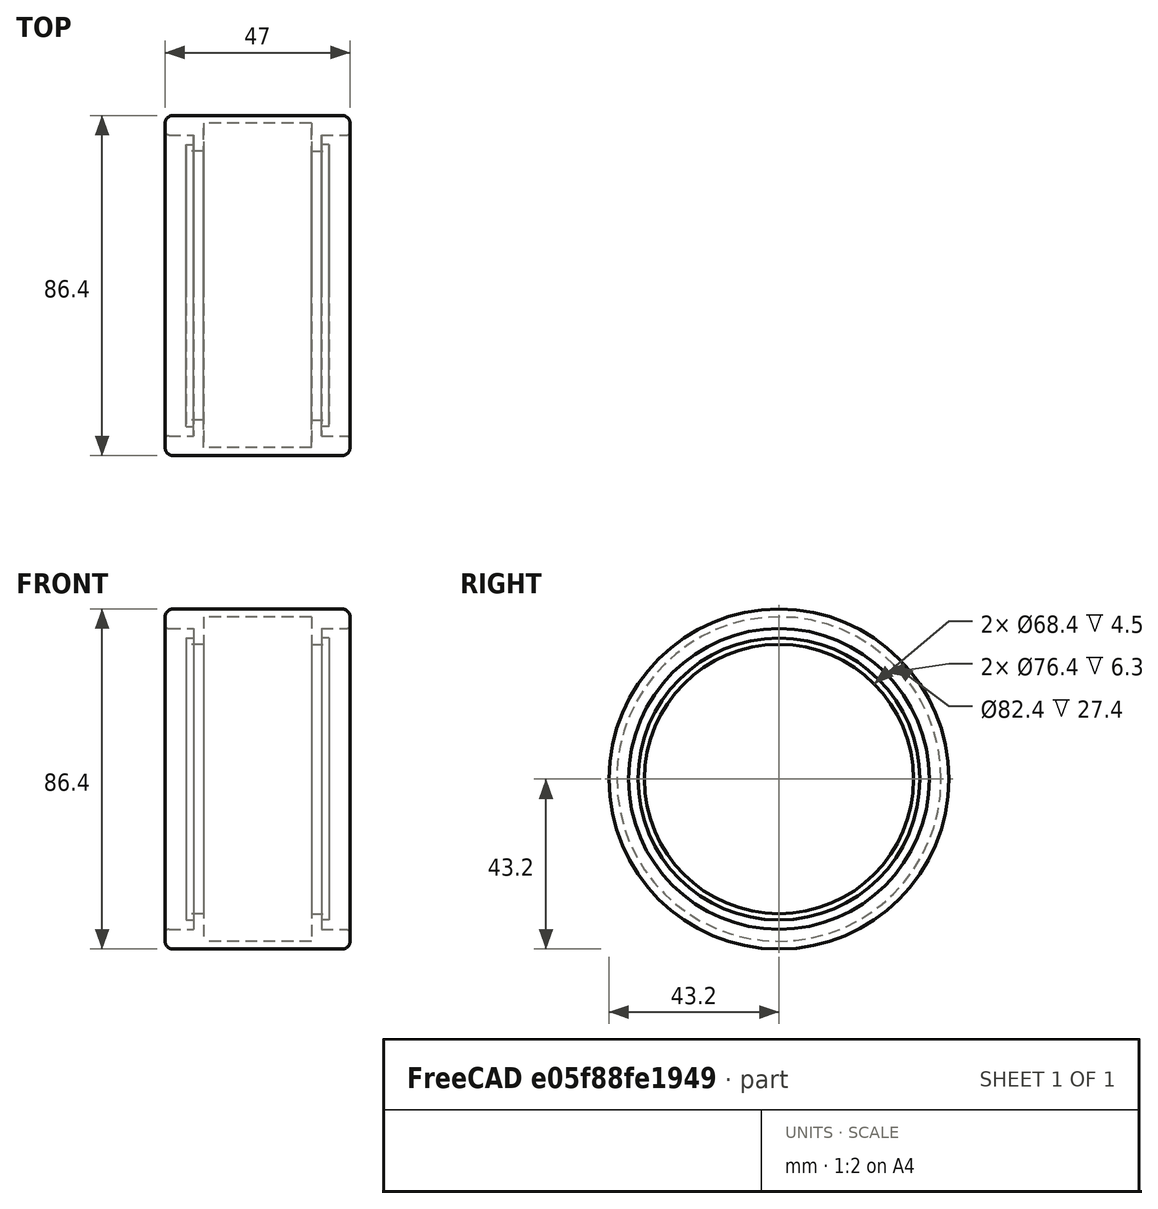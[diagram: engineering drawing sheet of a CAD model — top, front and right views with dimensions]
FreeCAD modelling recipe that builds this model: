
FCSTD DOCUMENT  (FreeCAD 0.17R13543 (Git))
Label: RacingTire
License: CreativeCommons Attribution-NonCommercial-ShareAlike
LicenseURL: http://creativecommons.org/licenses/by-nc-sa/4.0/
objects: Sketcher::SketchObject×1, PartDesign::Revolution×1, PartDesign::Body×1
note: 4 computed .brp shape members not serialized (recipe doc carries the construction recipe); baked Part::Feature solids carry a one-line shape summary decoded from their .brp

FEATURE [Sketcher::SketchObject] Sketch
  MapMode = 5
  Placement = pos=(0,0,0) rot=(1,0,0;1.5708rad)
  Support = -> [XZ_Plane]
  sketch-geometry (20):
    g0: LineSegment StartX=-13.7 StartY=41.2 StartZ=0 EndX=-13.7 EndY=34.2 EndZ=0
    g1: LineSegment StartX=-13.7 StartY=34.2 StartZ=0 EndX=-18.2 EndY=34.2 EndZ=0
    g2: LineSegment StartX=-18.2 StartY=34.2 StartZ=0 EndX=-18.2 EndY=35.8 EndZ=0
    g3: LineSegment StartX=-18.2 StartY=35.8 StartZ=0 EndX=-16.2 EndY=35.8 EndZ=0
    g4: LineSegment StartX=-16.2 StartY=35.8 StartZ=0 EndX=-16.2 EndY=38.2 EndZ=0
    g5: LineSegment StartX=-23.5 StartY=39.2 StartZ=0 EndX=-23.5 EndY=41.2 EndZ=0
    g6: ArcOfCircle CenterX=-21.5 CenterY=41.2 CenterZ=0 NormalX=0 NormalY=0 NormalZ=1 AngleXU=0 Radius=2 StartAngle=1.5708 EndAngle=3.14159
    g7: ArcOfCircle CenterX=-22.5 CenterY=39.2 CenterZ=0 NormalX=0 NormalY=0 NormalZ=1 AngleXU=0 Radius=1 StartAngle=3.14159 EndAngle=4.71239
    g8: LineSegment StartX=-22.5 StartY=38.2 StartZ=0 EndX=-16.2 EndY=38.2 EndZ=0
    g9: ArcOfCircle CenterX=21.5 CenterY=41.2 CenterZ=0 NormalX=0 NormalY=0 NormalZ=1 AngleXU=0 Radius=2 StartAngle=0 EndAngle=1.5708
    g10: LineSegment StartX=13.7 StartY=41.2 StartZ=0 EndX=13.7 EndY=34.2 EndZ=0
    g11: LineSegment StartX=13.7 StartY=34.2 StartZ=0 EndX=18.2 EndY=34.2 EndZ=0
    g12: LineSegment StartX=18.2 StartY=34.2 StartZ=0 EndX=18.2 EndY=35.8 EndZ=0
    g13: LineSegment StartX=18.2 StartY=35.8 StartZ=0 EndX=16.2 EndY=35.8 EndZ=0
    g14: LineSegment StartX=16.2 StartY=35.8 StartZ=0 EndX=16.2 EndY=38.2 EndZ=0
    g15: LineSegment StartX=16.2 StartY=38.2 StartZ=0 EndX=22.5 EndY=38.2 EndZ=0
    g16: LineSegment StartX=23.5 StartY=41.2 StartZ=0 EndX=23.5 EndY=39.2 EndZ=0
    g17: ArcOfCircle CenterX=22.5 CenterY=39.2 CenterZ=0 NormalX=0 NormalY=0 NormalZ=1 AngleXU=0 Radius=1 StartAngle=4.71239 EndAngle=6.28319
    g18: LineSegment StartX=-21.5 StartY=43.2 StartZ=0 EndX=21.5 EndY=43.2 EndZ=0
    g19: LineSegment StartX=13.7 StartY=41.2 StartZ=0 EndX=-13.7 EndY=41.2 EndZ=0
  constraints (61):
    c: Vertical(g0)
    c: Coincident(g1,g0)
    c: Horizontal(g1)
    c: Coincident(g2,g1)
    c: Vertical(g2)
    c: Coincident(g3,g2)
    c: Horizontal(g3)
    c: Coincident(g4,g3)
    c: Vertical(g4)
    c: Vertical(g5)
    c: Coincident(g6,g5)
    c: Horizontal(g6,g5)
    c: Vertical(g6,g6)
    c: Coincident(g7,g5)
    c: Horizontal(g5,g7)
    c: Vertical(g7,g7)
    c: Coincident(g8,g7)
    c: Coincident(g8,g4)
    c: Horizontal(g8)
    c: DistanceY(g7,g7) = 1
    c: DistanceY(g2,g2) = 1.6
    c: DistanceX(g3,g3) = 2
    c: DistanceY(g4,g4) = 2.4
    c: DistanceX(g3,g0) = 2.5
    c: DistanceX(g8,g8) = 6.3
    c: DistanceY(g-1,g0) = 34.2
    c: DistanceX(g0,g-1) = 13.7
    c: DistanceX(g5,g6) = 2
    c: DistanceY(g5,g5) = 2
    c: Symmetric(g9,g6,g-2)
    c: Vertical(g9,g9)
    c: Horizontal(g9,g9)
    c: Symmetric(g9,g5,g-2)
    c: Symmetric(g10,g0,g-2)
    c: Vertical(g10)
    c: Coincident(g11,g10)
    c: Horizontal(g11)
    c: Coincident(g12,g11)
    c: Coincident(g13,g12)
    c: Horizontal(g13)
    c: Coincident(g14,g13)
    c: Vertical(g14)
    c: Coincident(g15,g14)
    c: Horizontal(g15)
    c: Coincident(g16,g9)
    c: Vertical(g16)
    c: Vertical(g12)
    c: Symmetric(g11,g1,g-2)
    c: Symmetric(g13,g3,g-2)
    c: Symmetric(g14,g4,g-2)
    c: Coincident(g17,g15)
    c: Coincident(g17,g16)
    c: Vertical(g17,g15)
    c: Horizontal(g17,g16)
    c: Symmetric(g15,g7,g-2)
    c: Coincident(g18,g6)
    c: Coincident(g18,g9)
    c: Horizontal(g18)
    c: Coincident(g19,g0)
    c: Coincident(g19,g10)
    c: DistanceY(g0,g6) = 2
FEATURE [PartDesign::Revolution] Revolution
  Angle = 360
  Axis = (1,0,0)
  Base = (0,0,0)
  Placement = pos=(0,0,0) rot=(1,0,0;1.5708rad)
  Profile = -> Sketch
  ReferenceAxis = -> X_Axis
FEATURE [PartDesign::Body] Body  label="Tire"
  Group = -> [Sketch,Revolution]
  Origin = -> Origin
  Tip = -> Revolution
